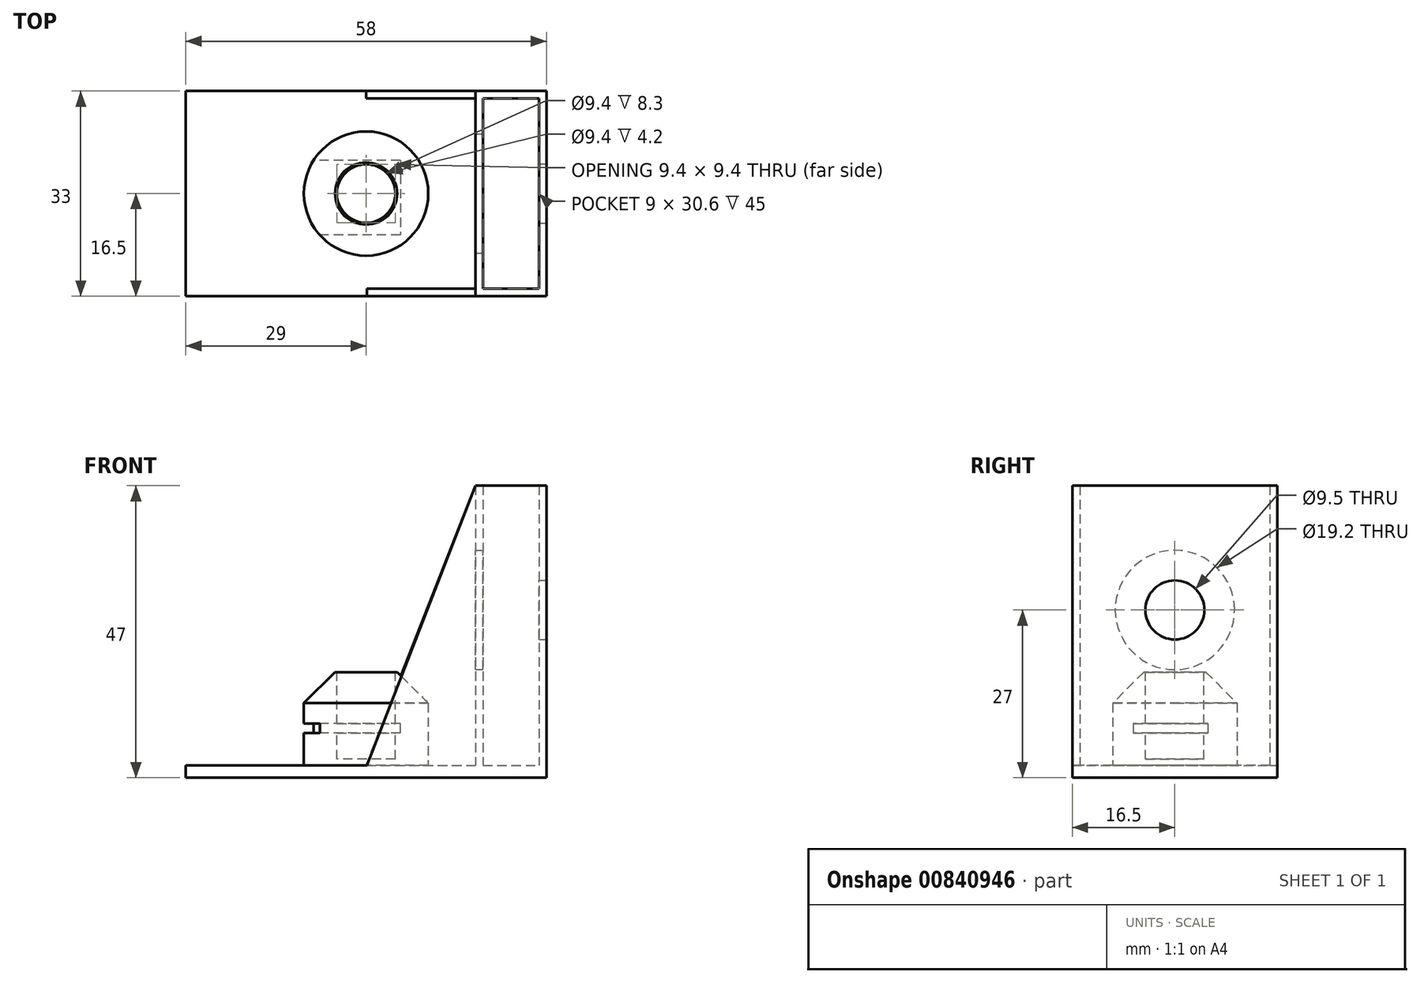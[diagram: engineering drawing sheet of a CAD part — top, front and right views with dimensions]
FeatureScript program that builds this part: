
annotation { "Feature Type Name" : "Feature", "Feature Type Description" : "" }
export const myFeature = defineFeature(function(context is Context, id is Id, definition is map)
    precondition{}
    {
        {
            var Q0;
            Q0=qCreatedBy(makeId("Top.planeOp"),FACE);
            var sketch = newSketch(context, id + "F0", { "sketchPlane" : qUnion([Q0])});
            skLineSegment(sketch, "E0.bottom", {"start": v(0, 0) * mm, "end": v(0, 0) * mm});
            skLineSegment(sketch, "E0.top", {"start": v(0, 33) * mm, "end": v(58, 33) * mm});
            skLineSegment(sketch, "E0.left", {"start": v(0, 0) * mm, "end": v(0, 33) * mm});
            skLineSegment(sketch, "E0.right", {"start": v(58, 0) * mm, "end": v(58, 33) * mm});
            skLineSegment(sketch, "E1.trimOffspring", {"start": v(58, 0) * mm, "end": v(58, 0) * mm});
            skLineSegment(sketch, "E2", {"start": v(29, 33) * mm, "end": v(29, -66) * mm, "construction": true});
            skLineSegment(sketch, "E3", {"start": v(0, 0) * mm, "end": v(58, 0) * mm});
            skSolve(sketch);
        }
        {
            var Q0;
            Q0 = qSketchRegion(id + "F0", true);
            extrude(context, id + "F1", {"entities" : qUnion([Q0]), "depth" : 2 * mm, "offsetDistance" : 25 * mm});
        }
        {
            var Q0;
            Q0=makeQuery(id+"F1.opExtrude","CAP_FACE",FACE,{"disambiguationData":[OSD([sQuery(id+"F0.wireOp",EDGE,"E0.bottom"),sQuery(id+"F0.wireOp",EDGE,"E0.top"),sQuery(id+"F0.wireOp",EDGE,"E0.left"),sQuery(id+"F0.wireOp",EDGE,"E0.right")])],"isStart":false});
            var sketch = newSketch(context, id + "F2", { "sketchPlane" : qUnion([Q0])});
            skCircle(sketch, "E4", {"center": v(29, 16.5) * mm, "radius": 10 * mm});
            skPoint(sketch, "E4.centerSnap0", {"position": v(58, 16.5) * mm});
            skPoint(sketch, "E4.centerSnap1", {"position": v(29, 33) * mm});
            skSolve(sketch);
        }
        {
            var Q0;
            Q0 = qSketchRegion(id + "F2", true);
            extrude(context, id + "F3", {"entities" : qUnion([Q0]), "operationType" : NewBodyOperationType.ADD, "depth" : 15 * mm, "offsetDistance" : 25 * mm});
        }
        {
            var Q0;
            Q0=makeQuery(id+"F3.opExtrude","CAP_FACE",FACE,{"disambiguationData":[OSD([sQuery(id+"F2.wireOp",EDGE,"E4")])],"isStart":false});
            var sketch = newSketch(context, id + "F4", { "sketchPlane" : qUnion([Q0])});
            skCircle(sketch, "E5", {"center": v(29, 16.5) * mm, "radius": 4.7 * mm});
            skSolve(sketch);
        }
        {
            var Q0;
            Q0 = qSketchRegion(id + "F4", true);
            extrude(context, id + "F5", {"entities" : qUnion([Q0]), "operationType" : NewBodyOperationType.REMOVE, "oppositeDirection" : true, "depth" : 14 * mm, "offsetDistance" : 25 * mm});
        }
        {
            var Q0;
            Q0=qCreatedBy(makeId("Right.planeOp"),FACE);
            var sketch = newSketch(context, id + "F6", { "sketchPlane" : qUnion([Q0])});
            skLineSegment(sketch, "E6.bottom", {"start": v(21.83, 7.2) * mm, "end": v(9.83, 7.2) * mm});
            skLineSegment(sketch, "E6.top", {"start": v(21.83, 8.7) * mm, "end": v(9.83, 8.7) * mm});
            skLineSegment(sketch, "E6.left", {"start": v(21.83, 7.2) * mm, "end": v(21.83, 8.7) * mm});
            skLineSegment(sketch, "E6.right", {"start": v(9.83, 7.2) * mm, "end": v(9.83, 8.7) * mm});
            skSolve(sketch);
        }
        {
            var Q0;
            Q0 = qSketchRegion(id + "F6", true);
            extrude(context, id + "F7", {"entities" : qUnion([Q0]), "operationType" : NewBodyOperationType.REMOVE, "depth" : 34.5 * mm, "offsetDistance" : 25 * mm});
        }
        {
            var Q0;
            Q0=makeQuery(id+"F1.opExtrude","CAP_FACE",FACE,{"disambiguationData":[OSD([sQuery(id+"F0.wireOp",EDGE,"E0.bottom"),sQuery(id+"F0.wireOp",EDGE,"E0.top"),sQuery(id+"F0.wireOp",EDGE,"E0.left"),sQuery(id+"F0.wireOp",EDGE,"E0.right")])],"isStart":false});
            var sketch = newSketch(context, id + "F8", { "sketchPlane" : qUnion([Q0])});
            skLineSegment(sketch, "E7.bottom", {"start": v(58, 33) * mm, "end": v(56.8, 33) * mm});
            skLineSegment(sketch, "E7.top", {"start": v(58, 0) * mm, "end": v(56.8, 0) * mm});
            skLineSegment(sketch, "E7.left", {"start": v(58, 33) * mm, "end": v(58, 0) * mm});
            skLineSegment(sketch, "E7.right", {"start": v(56.8, 33) * mm, "end": v(56.8, 0) * mm});
            skSolve(sketch);
        }
        {
            var Q0;
            Q0 = qSketchRegion(id + "F8", true);
            extrude(context, id + "F9", {"entities" : qUnion([Q0]), "operationType" : NewBodyOperationType.ADD, "depth" : 45 * mm, "offsetDistance" : 25 * mm});
        }
        {
            var Q0;
            Q0=makeQuery(id+"F9.boolean.opBoolean","MERGE",FACE,{"derivedFrom":[makeQuery(id+"F1.opExtrude","SWEPT_FACE",FACE,{"disambiguationData":[OSD([sQuery(id+"F0.wireOp",EDGE,"E0.right")])]}),makeQuery(id+"F9.opExtrude","SWEPT_FACE",FACE,{"disambiguationData":[OSD([sQuery(id+"F8.wireOp",EDGE,"E7.left")])]})]});
            var sketch = newSketch(context, id + "F10", { "sketchPlane" : qUnion([Q0])});
            skCircle(sketch, "E8", {"center": v(16.5, 27) * mm, "radius": 4.75 * mm});
            skPoint(sketch, "E8.centerSnap0", {"position": v(0, 23.5) * mm});
            skPoint(sketch, "E8.centerSnap1", {"position": v(16.5, 47) * mm});
            skSolve(sketch);
        }
        {
            var Q0;
            Q0 = qSketchRegion(id + "F10", true);
            extrude(context, id + "F11", {"entities" : qUnion([Q0]), "operationType" : NewBodyOperationType.REMOVE, "oppositeDirection" : true, "depth" : 20 * mm, "offsetDistance" : 25 * mm});
        }
        {
            var Q0;
            Q0=makeQuery(id+"F1.opExtrude","CAP_FACE",FACE,{"disambiguationData":[OSD([sQuery(id+"F0.wireOp",EDGE,"E0.bottom"),sQuery(id+"F0.wireOp",EDGE,"E0.top"),sQuery(id+"F0.wireOp",EDGE,"E0.left"),sQuery(id+"F0.wireOp",EDGE,"E0.right")])],"isStart":false});
            var sketch = newSketch(context, id + "F12", { "sketchPlane" : qUnion([Q0])});
            skLineSegment(sketch, "E9.bottom", {"start": v(47.8, 33) * mm, "end": v(46.6, 33) * mm});
            skLineSegment(sketch, "E9.top", {"start": v(47.8, 0) * mm, "end": v(46.6, 0) * mm});
            skLineSegment(sketch, "E9.left", {"start": v(47.8, 33) * mm, "end": v(47.8, 0) * mm});
            skLineSegment(sketch, "E9.right", {"start": v(46.6, 33) * mm, "end": v(46.6, 0) * mm});
            skSolve(sketch);
        }
        {
            var Q0;
            Q0 = qSketchRegion(id + "F12", true);
            extrude(context, id + "F13", {"entities" : qUnion([Q0]), "operationType" : NewBodyOperationType.ADD, "depth" : 45 * mm, "offsetDistance" : 25 * mm});
        }
        {
            var Q0;
            Q0=makeQuery(id+"F13.opExtrude","SWEPT_FACE",FACE,{"disambiguationData":[OSD([sQuery(id+"F12.wireOp",EDGE,"E9.left")])]});
            var sketch = newSketch(context, id + "F14", { "sketchPlane" : qUnion([Q0])});
            skCircle(sketch, "E10", {"center": v(16.5, 27) * mm, "radius": 9.6 * mm});
            skSolve(sketch);
        }
        {
            var Q0;
            Q0 = qSketchRegion(id + "F14", true);
            extrude(context, id + "F15", {"entities" : qUnion([Q0]), "operationType" : NewBodyOperationType.REMOVE, "oppositeDirection" : true, "depth" : 10 * mm, "offsetDistance" : 25 * mm});
        }
        {
            var Q0;
            Q0=qCreatedBy(makeId("Front.planeOp"),FACE);
            var sketch = newSketch(context, id + "F16", { "sketchPlane" : qUnion([Q0])});
            skLineSegment(sketch, "E11", {"start": v(46.6, 47) * mm, "end": v(29.1, 2) * mm});
            skPoint(sketch, "E11.endSnap0", {"position": v(29.1, 0) * mm});
            skLineSegment(sketch, "E12", {"start": v(29.1, 2) * mm, "end": v(46.6, 2) * mm});
            skLineSegment(sketch, "E13", {"start": v(46.6, 2) * mm, "end": v(46.6, 47) * mm});
            skSolve(sketch);
        }
        {
            var Q0;
            Q0 = qSketchRegion(id + "F16", true);
            extrude(context, id + "F17", {"entities" : qUnion([Q0]), "operationType" : NewBodyOperationType.ADD, "oppositeDirection" : true, "depth" : 1.2 * mm, "offsetDistance" : 25 * mm});
        }
        {
            var Q0;
            Q0=makeQuery(id+"F13.boolean.opBoolean","MERGE",FACE,{"derivedFrom":[makeQuery(id+"F9.boolean.opBoolean","MERGE",FACE,{"derivedFrom":[makeQuery(id+"F1.opExtrude","SWEPT_FACE",FACE,{"disambiguationData":[OSD([sQuery(id+"F0.wireOp",EDGE,"E0.top")])]}),makeQuery(id+"F9.opExtrude","SWEPT_FACE",FACE,{"disambiguationData":[OSD([sQuery(id+"F8.wireOp",EDGE,"E7.bottom")])]})]}),makeQuery(id+"F13.opExtrude","SWEPT_FACE",FACE,{"disambiguationData":[OSD([sQuery(id+"F12.wireOp",EDGE,"E9.bottom")])]})]});
            var sketch = newSketch(context, id + "F18", { "sketchPlane" : qUnion([Q0])});
            skLineSegment(sketch, "E14", {"start": v(-46.6, 47) * mm, "end": v(-46.6, 2) * mm});
            skLineSegment(sketch, "E15", {"start": v(-46.6, 2) * mm, "end": v(-29, 2) * mm});
            skPoint(sketch, "E15.endSnap0", {"position": v(-29, 0) * mm});
            skLineSegment(sketch, "E16", {"start": v(-29, 2) * mm, "end": v(-46.6, 47) * mm});
            skSolve(sketch);
        }
        {
            var Q0;
            Q0=makeQuery(id+"F18.imprint","IMPRINT",FACE,{"disambiguationData":[TD([[makeQuery(id+"F18.imprint","IMPRINT",EDGE,{"derivedFrom":sQuery(id+"F18.wireOp",EDGE,"E14")}),1.0]])]});
            extrude(context, id + "F19", {"entities" : qUnion([Q0]), "operationType" : NewBodyOperationType.ADD, "oppositeDirection" : true, "depth" : 1.2 * mm, "offsetDistance" : 25 * mm});
        }
        {
            var Q0;
            Q0=qCreatedBy(makeId("Front.planeOp"),FACE);
            var sketch = newSketch(context, id + "F20", { "sketchPlane" : qUnion([Q0])});
            skLineSegment(sketch, "E17.bottom", {"start": v(47.8, 47) * mm, "end": v(56.8, 47) * mm});
            skLineSegment(sketch, "E17.top", {"start": v(47.8, 2) * mm, "end": v(56.8, 2) * mm});
            skLineSegment(sketch, "E17.left", {"start": v(47.8, 47) * mm, "end": v(47.8, 2) * mm});
            skLineSegment(sketch, "E17.right", {"start": v(56.8, 47) * mm, "end": v(56.8, 2) * mm});
            skSolve(sketch);
        }
        {
            var Q0;
            Q0 = qSketchRegion(id + "F20", true);
            extrude(context, id + "F21", {"entities" : qUnion([Q0]), "operationType" : NewBodyOperationType.ADD, "oppositeDirection" : true, "depth" : 1.2 * mm, "offsetDistance" : 25 * mm});
        }
        {
            var Q0;
            Q0=makeQuery(id+"F19.boolean.opBoolean","MERGE",FACE,{"derivedFrom":[makeQuery(id+"F13.boolean.opBoolean","MERGE",FACE,{"derivedFrom":[makeQuery(id+"F9.boolean.opBoolean","MERGE",FACE,{"derivedFrom":[makeQuery(id+"F1.opExtrude","SWEPT_FACE",FACE,{"disambiguationData":[OSD([sQuery(id+"F0.wireOp",EDGE,"E0.top")])]}),makeQuery(id+"F9.opExtrude","SWEPT_FACE",FACE,{"disambiguationData":[OSD([sQuery(id+"F8.wireOp",EDGE,"E7.bottom")])]})]}),makeQuery(id+"F13.opExtrude","SWEPT_FACE",FACE,{"disambiguationData":[OSD([sQuery(id+"F12.wireOp",EDGE,"E9.bottom")])]})]}),makeQuery(id+"F19.opExtrude","CAP_FACE",FACE,{"disambiguationData":[OSD([sQuery(id+"F18.wireOp",EDGE,"E14"),sQuery(id+"F18.wireOp",EDGE,"E15"),sQuery(id+"F18.wireOp",EDGE,"E16")])],"isStart":true})]});
            var sketch = newSketch(context, id + "F22", { "sketchPlane" : qUnion([Q0])});
            skLineSegment(sketch, "E18.bottom", {"start": v(-56.8, 47) * mm, "end": v(-47.8, 47) * mm});
            skLineSegment(sketch, "E18.top", {"start": v(-56.8, 2) * mm, "end": v(-47.8, 2) * mm});
            skLineSegment(sketch, "E18.left", {"start": v(-56.8, 47) * mm, "end": v(-56.8, 2) * mm});
            skLineSegment(sketch, "E18.right", {"start": v(-47.8, 47) * mm, "end": v(-47.8, 2) * mm});
            skSolve(sketch);
        }
        {
            var Q0;
            Q0 = qSketchRegion(id + "F22", true);
            extrude(context, id + "F23", {"entities" : qUnion([Q0]), "operationType" : NewBodyOperationType.ADD, "oppositeDirection" : true, "depth" : 1.2 * mm, "offsetDistance" : 25 * mm});
        }
        {
            var Q0;
            Q0=makeQuery(id+"F3.opExtrude","CAP_EDGE",EDGE,{"disambiguationData":[OSD([sQuery(id+"F2.wireOp",EDGE,"E4")])],"isStart":false});
            chamfer(context, id + "F24", {"entities" : qUnion([Q0]), "width" : 5 * mm, "tangentPropagation" : true});
        }
    });
